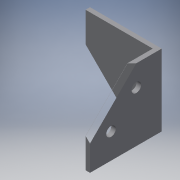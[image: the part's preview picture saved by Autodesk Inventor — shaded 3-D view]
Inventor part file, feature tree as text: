
AUTODESK INVENTOR PART (.ipt)
format: ipt  version: 2016 (Build 200138000, 138)  size: 134,656 bytes
history: native  units: in
note: dims shown in document units (in); Inventor stores cm internally (conversion verified against a paired STEP export)
features: extrude x4, sketch x4
ambient origin geometry x8: Origin, YZ Plane, XZ Plane, XY Plane, X Axis, Y Axis, Z Axis, Center Point
bodies: Solid1 (feature_tree)
feature tree (8):
  extrude  "Extrusion1"  Depth=0.125in
  extrude  "Extrusion3"  Depth=1.875in
  extrude  "Extrusion4"  Depth=2.0in
  extrude  "Extrusion5"  Depth=0.125in TaperAngle=0.0deg
  sketch  "Sketch1"  dims[d0=2.0in d1=0.125in]
  sketch  "Sketch2"  dims[d2=1.875in d3=1.875in]
  sketch  "Sketch3"  dims[d4=2.0in d5=0.0in d6=2.0in]
  sketch  "Sketch4"  dims[d7=45.0deg d16=0.125in d17=0.0in d18=0.2656in d19=0.2656in d20=0.5in d21=0.5in d22=1.0in d23=0.8284in d24=0.125in d25=0.0in d26=0.2656in d27=0.5in d28=0.5in d29=0.5in d30=1.5in d31=0.125in d32=0.0in]
